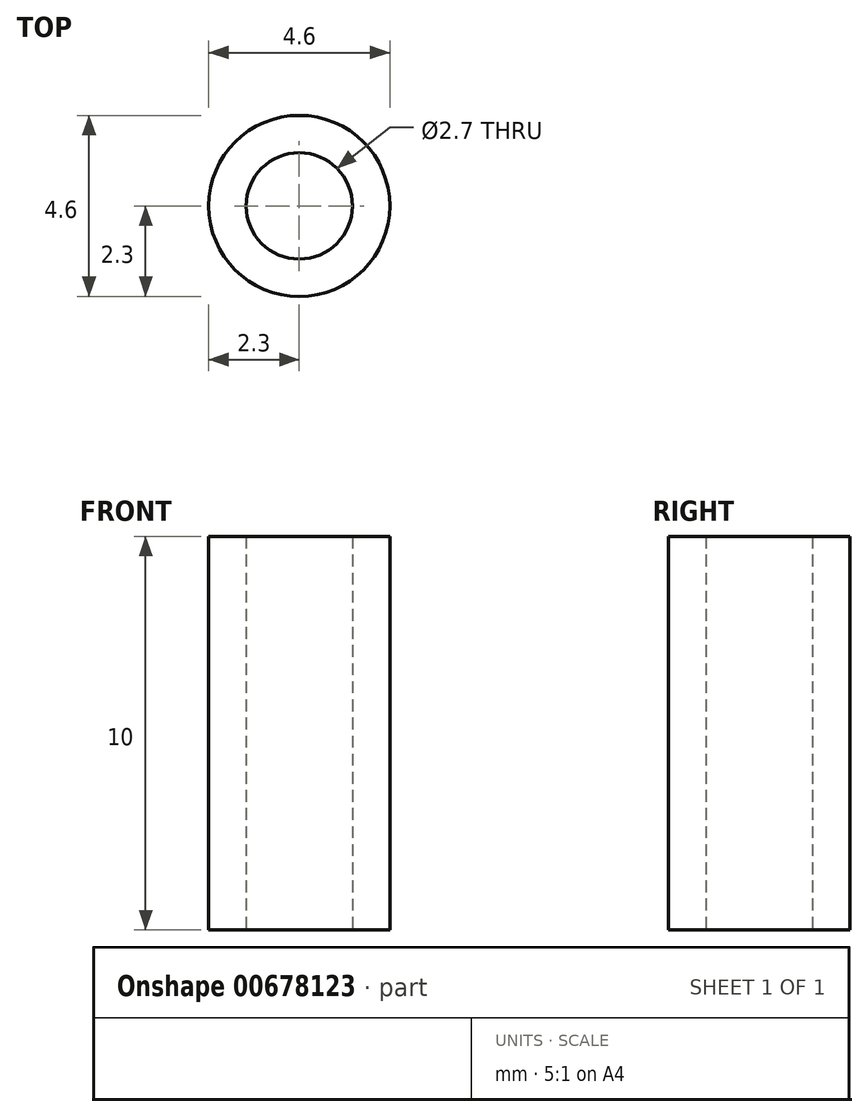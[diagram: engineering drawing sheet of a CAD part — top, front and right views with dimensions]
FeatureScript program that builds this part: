
annotation { "Feature Type Name" : "Feature", "Feature Type Description" : "" }
export const myFeature = defineFeature(function(context is Context, id is Id, definition is map)
    precondition{}
    {
        {
            var Q0;
            Q0=qCreatedBy(makeId("Top.planeOp"),FACE);
            var sketch = newSketch(context, id + "F0", { "sketchPlane" : qUnion([Q0])});
            skCircle(sketch, "E0", {"center": v(0, 0) * mm, "radius": 2.3 * mm});
            skCircle(sketch, "E1", {"center": v(0, 0) * mm, "radius": 1.35 * mm});
            skSolve(sketch);
        }
        {
            var Q0;
            Q0=makeQuery(id+"F0.imprint","IMPRINT",FACE,{"disambiguationData":[TD([[makeQuery(id+"F0.imprint","IMPRINT",EDGE,{"derivedFrom":sQuery(id+"F0.wireOp",EDGE,"E0")}),1.0]])]});
            extrude(context, id + "F1", {"entities" : qUnion([Q0]), "depth" : 10 * mm, "offsetDistance" : 25 * mm});
        }
    });
